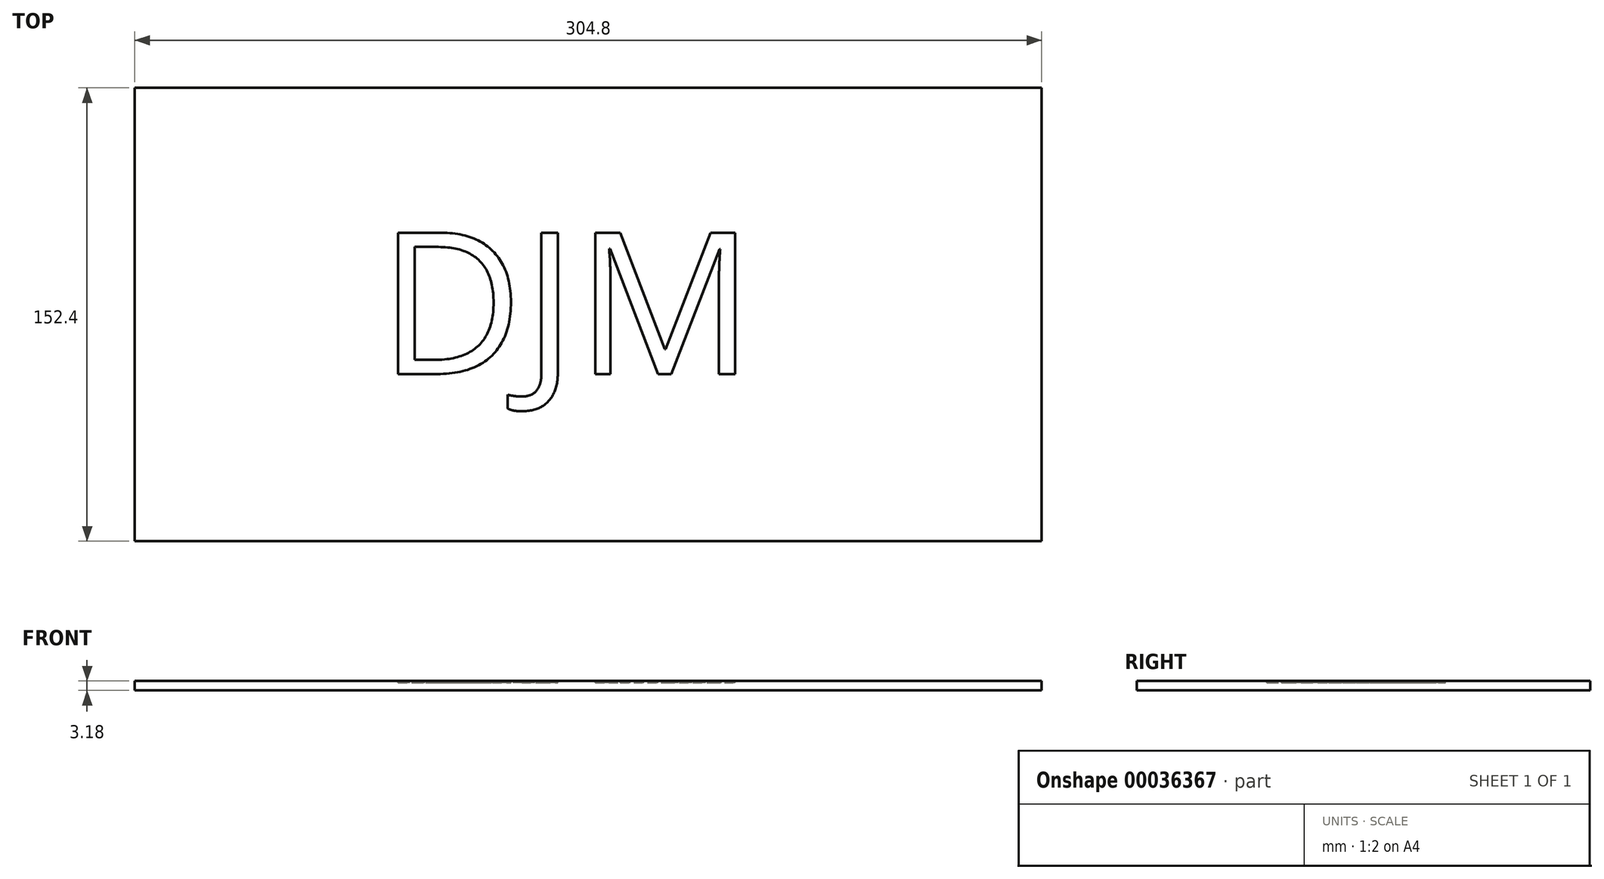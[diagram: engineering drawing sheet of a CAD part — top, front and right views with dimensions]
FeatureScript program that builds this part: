
annotation { "Feature Type Name" : "Feature", "Feature Type Description" : "" }
export const myFeature = defineFeature(function(context is Context, id is Id, definition is map)
    precondition{}
    {
        {
            var Q0;
            Q0=qCreatedBy(makeId("Top.planeOp"),FACE);
            var sketch = newSketch(context, id + "F0", { "sketchPlane" : qUnion([Q0])});
            skLineSegment(sketch, "E0.bottom", {"start": v(-65.56, 10.76) * mm, "end": v(239.24, 10.76) * mm});
            skLineSegment(sketch, "E0.top", {"start": v(-65.56, -141.64) * mm, "end": v(239.24, -141.64) * mm});
            skLineSegment(sketch, "E0.left", {"start": v(-65.56, 10.76) * mm, "end": v(-65.56, -141.64) * mm});
            skLineSegment(sketch, "E0.right", {"start": v(239.24, 10.76) * mm, "end": v(239.24, -141.64) * mm});
            skSolve(sketch);
        }
        {
            var Q0;
            Q0=makeQuery(id+"F0.imprint","IMPRINT",FACE,{"disambiguationData":[TD([[makeQuery(id+"F0.imprint","IMPRINT",EDGE,{"derivedFrom":sQuery(id+"F0.wireOp",EDGE,"E0.bottom")}),-1.0]])]});
            extrude(context, id + "F1", {"entities" : qUnion([Q0]), "depth" : 3.17 * mm});
        }
        {
            var Q0;
            Q0=makeQuery(id+"F1.opExtrude","CAP_FACE",FACE,{"disambiguationData":[OSD([sQuery(id+"F0.wireOp",EDGE,"E0.bottom"),sQuery(id+"F0.wireOp",EDGE,"E0.top"),sQuery(id+"F0.wireOp",EDGE,"E0.left"),sQuery(id+"F0.wireOp",EDGE,"E0.right")])],"isStart":false});
            var sketch = newSketch(context, id + "F2", { "sketchPlane" : qUnion([Q0])});
            skText(sketch, "E1", { "text": "DJM", "fontName": "OpenSans-Regular.ttf"});
            const initialGuessF2  = {"E1": [0.01643, -0.08543, 1, 0, 0.0479]};
            skSetInitialGuess(sketch, initialGuessF2);
            skSolve(sketch);
        }
        {
            var Q0;
            Q0 = qSketchRegion(id + "F2", true);
            extrude(context, id + "F3", {"entities" : qUnion([Q0]), "operationType" : NewBodyOperationType.REMOVE, "oppositeDirection" : true, "depth" : 0.64 * mm});
        }
    });
